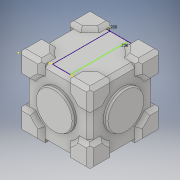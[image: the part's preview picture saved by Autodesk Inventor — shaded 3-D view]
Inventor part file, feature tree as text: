
AUTODESK INVENTOR PART (.ipt)
format: ipt  version: 2018 (Build 220112000, 112)  size: 701,440 bytes
history: native  units: in
note: dims shown in document units (in); Inventor stores cm internally (conversion verified against a paired STEP export)
features: chamfer x100, sketch x16, extrude x15
ambient origin geometry x8: Origin, YZ Plane, XZ Plane, XY Plane, X Axis, Y Axis, Z Axis, Center Point
bodies: Solid1 (feature_tree)
feature tree (131):
  extrude  "Extrusion1"  Depth=4.0in
  extrude  "Extrusion2"  Depth=4.0in
  extrude  "Extrusion3"  Depth=1.3in
  extrude  "Extrusion4"  Depth=1.3in
  extrude  "Extrusion5"  Depth=1.3in
  extrude  "Extrusion6"  Depth=0.2in
  chamfer  "Chamfer42"  Distance=0.2in
  chamfer  "Chamfer43"  Distance=0.2in
  chamfer  "Chamfer44"  Distance=0.2in
  chamfer  "Chamfer45"  Distance=0.2in
  chamfer  "Chamfer46"  Distance=0.2in Angle=45.0deg
  chamfer  "Chamfer47"  Distance=0.2in Angle=45.0deg
  chamfer  "Chamfer48"  Distance=0.2in Angle=45.0deg
  chamfer  "Chamfer49"  Distance=0.2in Angle=45.0deg
  chamfer  "Chamfer50"  Distance=0.2in Angle=45.0deg
  chamfer  "Chamfer51"  Distance=0.2in Angle=45.0deg
  chamfer  "Chamfer52"  Distance=0.2in Angle=45.0deg
  chamfer  "Chamfer53"  Distance=0.2in Angle=45.0deg
  chamfer  "Chamfer54"  Distance=0.2in Angle=45.0deg
  chamfer  "Chamfer55"  Distance=0.2in Angle=45.0deg
  chamfer  "Chamfer56"  Distance=0.2in Angle=45.0deg
  chamfer  "Chamfer57"  Distance=0.2in Angle=45.0deg
  chamfer  "Chamfer58"  Distance=0.2in Angle=45.0deg
  chamfer  "Chamfer59"  Distance=0.2in Angle=45.0deg
  chamfer  "Chamfer60"  Distance=0.2in Angle=45.0deg
  chamfer  "Chamfer61"  Distance=0.2in Angle=45.0deg
  chamfer  "Chamfer62"  Distance=0.2in Angle=45.0deg
  chamfer  "Chamfer63"  Distance=0.2in Angle=45.0deg
  chamfer  "Chamfer64"  Distance=0.2in Angle=45.0deg
  chamfer  "Chamfer65"  Distance=0.2in Angle=45.0deg
  chamfer  "Chamfer66"  Distance=0.2in Angle=45.0deg
  chamfer  "Chamfer67"  Distance=0.2in Angle=45.0deg
  chamfer  "Chamfer68"  Distance=0.2in Angle=45.0deg
  chamfer  "Chamfer69"  Distance=0.2in Angle=45.0deg
  chamfer  "Chamfer70"  Distance=0.2in Angle=45.0deg
  chamfer  "Chamfer71"  Distance=0.2in Angle=45.0deg
  chamfer  "Chamfer72"  Distance=0.2in Angle=45.0deg
  chamfer  "Chamfer73"  Distance=0.2in Angle=45.0deg
  chamfer  "Chamfer74"  Distance=0.2in Angle=45.0deg
  chamfer  "Chamfer75"  Distance=0.2in Angle=45.0deg
  chamfer  "Chamfer76"  Distance=0.2in Angle=45.0deg
  chamfer  "Chamfer77"  Distance=0.2in Angle=45.0deg
  chamfer  "Chamfer78"  Distance=0.2in Angle=45.0deg
  chamfer  "Chamfer79"  Distance=0.2in Angle=45.0deg
  chamfer  "Chamfer80"  Distance=0.2in Angle=45.0deg
  chamfer  "Chamfer81"  Distance=0.2in Angle=45.0deg
  chamfer  "Chamfer82"  Distance=0.2in Angle=45.0deg
  chamfer  "Chamfer83"  Distance=0.2in Angle=45.0deg
  chamfer  "Chamfer84"  Distance=0.2in Angle=45.0deg
  chamfer  "Chamfer85"  Distance=0.2in Angle=45.0deg
  chamfer  "Chamfer86"  Distance=0.2in Angle=45.0deg
  chamfer  "Chamfer87"  Distance=0.2in Angle=45.0deg
  chamfer  "Chamfer88"  Distance=0.2in Angle=45.0deg
  chamfer  "Chamfer89"  Distance=0.2in Angle=45.0deg
  chamfer  "Chamfer90"  Distance=0.2in Angle=45.0deg
  chamfer  "Chamfer91"  Distance=0.2in Angle=45.0deg
  chamfer  "Chamfer92"  Distance=0.2in Angle=45.0deg
  chamfer  "Chamfer93"  Distance=0.2in Angle=45.0deg
  chamfer  "Chamfer94"  Distance=0.2in Angle=45.0deg
  chamfer  "Chamfer95"  Distance=0.2in Angle=45.0deg
  chamfer  "Chamfer96"  Distance=0.2in Angle=45.0deg
  chamfer  "Chamfer97"  Distance=0.2in Angle=45.0deg
  chamfer  "Chamfer98"  Distance=0.2in Angle=45.0deg
  chamfer  "Chamfer99"  Distance=0.2in Angle=45.0deg
  chamfer  "Chamfer100"  Distance=0.2in Angle=45.0deg
  chamfer  "Chamfer101"  Distance=0.2in Angle=45.0deg
  chamfer  "Chamfer102"  Distance=0.2in Angle=45.0deg
  chamfer  "Chamfer103"  Distance=0.2in Angle=45.0deg
  chamfer  "Chamfer104"  Distance=0.2in Angle=45.0deg
  chamfer  "Chamfer105"  Distance=0.2in Angle=45.0deg
  chamfer  "Chamfer106"  Distance=0.2in Angle=45.0deg
  chamfer  "Chamfer107"  Distance=0.2in Angle=45.0deg
  chamfer  "Chamfer108"  Distance=0.2in Angle=45.0deg
  chamfer  "Chamfer109"  Distance=0.2in Angle=45.0deg
  chamfer  "Chamfer110"  Distance=0.2in Angle=45.0deg
  chamfer  "Chamfer111"  Distance=0.2in Angle=45.0deg
  chamfer  "Chamfer112"  Distance=0.2in Angle=45.0deg
  chamfer  "Chamfer113"  Distance=0.2in Angle=45.0deg
  chamfer  "Chamfer114"  Distance=0.2in Angle=45.0deg
  chamfer  "Chamfer115"  Distance=0.2in Angle=45.0deg
  chamfer  "Chamfer116"  Distance=0.2in Angle=45.0deg
  chamfer  "Chamfer117"  Distance=0.2in Angle=45.0deg
  extrude  "Extrusion7"  Depth=0.2in TaperAngle=45.0deg
  extrude  "Extrusion8"  Depth=0.2in TaperAngle=45.0deg
  extrude  "Extrusion9"  Depth=0.2in TaperAngle=0.0deg
  extrude  "Extrusion10"  Depth=0.2in TaperAngle=0.0deg
  chamfer  "Chamfer118"  Distance=0.2in
  chamfer  "Chamfer119"  Distance=0.2in
  chamfer  "Chamfer120"  Distance=0.2in Angle=45.0deg
  chamfer  "Chamfer121"  Distance=0.2in Angle=45.0deg
  chamfer  "Chamfer122"  Distance=0.2in Angle=45.0deg
  chamfer  "Chamfer123"  Distance=0.2in Angle=45.0deg
  chamfer  "Chamfer124"  Distance=0.2in Angle=45.0deg
  chamfer  "Chamfer125"  Distance=0.2in Angle=45.0deg
  chamfer  "Chamfer126"  Distance=0.2in Angle=45.0deg
  chamfer  "Chamfer127"  Distance=0.2in Angle=45.0deg
  chamfer  "Chamfer128"  Distance=0.2in Angle=45.0deg
  chamfer  "Chamfer129"  Distance=0.2in Angle=45.0deg
  chamfer  "Chamfer130"  Distance=0.2in Angle=45.0deg
  chamfer  "Chamfer131"  Distance=0.2in Angle=45.0deg
  chamfer  "Chamfer132"  Distance=0.2in Angle=45.0deg
  chamfer  "Chamfer133"  Distance=0.2in Angle=45.0deg
  extrude  "Extrusion11"  Depth=0.2in TaperAngle=45.0deg
  chamfer  "Chamfer134"  Distance=2.8in
  chamfer  "Chamfer135"  Distance=0.2in
  chamfer  "Chamfer136"  Distance=0.2in Angle=45.0deg
  chamfer  "Chamfer137"  Distance=0.2in Angle=45.0deg
  extrude  "Extrusion12"  Depth=0.2in TaperAngle=45.0deg
  sketch  "Sketch16"  dims[d379=2.8in d380=0.2in d381=0.0in]
  sketch  "Sketch17"  dims[d382=2.8in d383=0.2in d384=0.0in]
  extrude  "Extrusion13"  Depth=0.2in TaperAngle=45.0deg
  extrude  "Extrusion14"  Depth=0.2in
  extrude  "Extrusion15"  Depth=0.2in TaperAngle=0.0deg
  chamfer  "Chamfer138"  Distance=2.1in
  chamfer  "Chamfer139"  Distance=2.1in
  chamfer  "Chamfer140"  Distance=2.1in
  chamfer  "Chamfer141"  Distance=0.2in
  sketch  "Sketch19"  dims[d430=0.2in d431=0.2in d432=45.0deg d433=0.2in d434=0.2in d435=45.0deg d436=2.8in d437=0.2in d438=0.0in d439=0.2in d440=0.2in d441=45.0deg d442=0.2in d443=0.2in d444=45.0deg d445=0.2in d446=0.2in d447=45.0deg d448=0.2in d449=0.2in d450=45.0deg d451=2.1in d452=0.2in d453=0.0in d454=2.1in d455=2.1in d456=2.1in d457=0.2in d458=0.0in d459=0.2in d460=0.0in d461=0.2in d462=0.0in d463=0.05in d464=0.1in d465=45.0deg d466=0.05in d467=0.1in d468=45.0deg d469=0.05in d470=0.1in d471=45.0deg d472=0.05in d473=0.1in d474=45.0deg d475=0.2in d476=0.2in]
  sketch  "Sketch1"  dims[d0=4.0in d1=4.0in]
  sketch  "Sketch2"  dims[d2=4.0in d3=0.0in d4=1.3in]
  sketch  "Sketch3"  dims[d5=1.3in d6=1.3in]
  sketch  "Sketch4"  dims[d7=1.3in d8=1.3in]
  sketch  "Sketch5"  dims[d9=1.3in d10=1.3in]
  sketch  "Sketch6"  dims[d11=0.2in d12=0.0in d13=1.3in]
  sketch  "Sketch9"  dims[d14=1.3in]
  sketch  "Sketch11"  dims[d15=1.3in]
  sketch  "Sketch12"  dims[d16=1.3in d17=0.2in d18=0.0in d19=0.2in d20=0.0in d21=0.2in d22=0.0in d23=0.2in d24=0.0in d148=0.2in d149=0.2in d150=45.0deg d151=0.2in d152=0.2in d153=45.0deg d154=0.2in d155=0.2in d156=45.0deg d157=0.2in d158=0.2in d159=45.0deg d160=0.2in d161=0.2in d162=45.0deg d163=0.2in d164=0.2in d165=45.0deg d166=0.2in d167=0.2in d168=45.0deg d169=0.2in d170=0.2in d171=45.0deg d172=0.2in d173=0.2in d174=45.0deg d175=0.2in d176=0.2in d177=45.0deg d178=0.2in d179=0.2in d180=45.0deg d181=0.2in d182=0.2in d183=45.0deg d184=0.2in d185=0.2in d186=45.0deg d187=0.2in d188=0.2in d189=45.0deg d190=0.2in d191=0.2in d192=45.0deg d193=0.2in d194=0.2in d195=45.0deg d196=0.2in d197=0.2in d198=45.0deg d199=0.2in d200=0.2in d201=45.0deg d202=0.2in d203=0.2in d204=45.0deg d205=0.2in d206=0.2in d207=45.0deg d208=0.2in d209=0.2in d210=45.0deg d211=0.2in d212=0.2in d213=45.0deg d214=0.2in d215=0.2in d216=45.0deg d217=0.2in d218=0.2in d219=45.0deg d220=0.2in d221=0.2in d222=45.0deg d223=0.2in d224=0.2in d225=45.0deg d226=0.2in d227=0.2in d228=45.0deg d229=0.2in d230=0.2in d231=45.0deg d232=0.2in d233=0.2in d234=45.0deg d235=0.2in d236=0.2in d237=45.0deg d238=0.2in d239=0.2in d240=45.0deg d241=0.2in d242=0.2in d243=45.0deg d244=0.2in d245=0.2in d246=45.0deg d247=0.2in d248=0.2in d249=45.0deg d250=0.2in d251=0.2in d252=45.0deg d253=0.2in d254=0.2in d255=45.0deg d256=0.2in d257=0.2in d258=45.0deg d259=0.2in d260=0.2in d261=45.0deg d262=0.2in d263=0.2in d264=45.0deg d265=0.2in d266=0.2in d267=45.0deg d268=0.2in d269=0.2in d270=45.0deg d271=0.2in d272=0.2in d273=45.0deg d274=0.2in d275=0.2in d276=45.0deg d277=0.2in d278=0.2in d279=45.0deg d280=0.2in d281=0.2in d282=45.0deg d283=0.2in d284=0.2in d285=45.0deg d286=0.2in d287=0.2in d288=45.0deg d289=0.2in d290=0.2in d291=45.0deg d292=0.2in d293=0.2in d294=45.0deg d295=0.2in d296=0.2in d297=45.0deg d298=0.2in d299=0.2in d300=45.0deg d301=0.2in d302=0.2in d303=45.0deg d304=0.2in d305=0.2in d306=45.0deg d307=0.2in d308=0.2in d309=45.0deg d310=0.2in d311=0.2in d312=45.0deg d313=0.2in d314=0.2in d315=45.0deg d316=0.2in d317=0.2in d318=45.0deg d319=0.2in d320=0.2in d321=45.0deg d322=0.2in d323=0.2in d324=45.0deg d325=0.2in d326=0.2in d327=45.0deg d328=0.2in d329=0.2in d330=45.0deg d331=0.2in d332=0.2in d333=45.0deg d334=0.2in d335=0.2in d336=45.0deg d337=0.2in d338=0.2in d339=45.0deg d340=0.2in d341=0.2in d342=45.0deg d343=0.2in d344=0.2in d345=45.0deg d346=0.2in d347=0.2in d348=45.0deg d349=0.2in d350=0.2in d351=45.0deg d352=0.2in d353=0.2in d354=45.0deg d355=0.2in d356=0.2in d357=45.0deg d358=0.2in d359=0.2in d360=45.0deg d361=0.2in d362=0.2in d363=45.0deg]
  sketch  "Sketch13"  dims[d364=0.2in d365=0.2in d366=45.0deg d367=0.2in d368=0.2in d369=45.0deg]
  sketch  "Sketch14"  dims[d370=0.2in d371=0.2in d372=45.0deg d373=0.2in d374=0.2in d375=45.0deg]
  sketch  "Sketch15"  dims[d376=2.8in d377=0.2in d378=0.0in]
  sketch  "Sketch18"  dims[d385=2.8in d386=0.2in d387=0.0in d388=0.2in d389=0.2in d390=45.0deg d391=0.2in d392=0.2in d393=45.0deg d394=0.2in d395=0.2in d396=45.0deg d397=0.2in d398=0.2in d399=45.0deg d400=0.2in d401=0.2in d402=45.0deg d403=0.2in d404=0.2in d405=45.0deg d406=0.2in d407=0.2in d408=45.0deg d409=0.2in d410=0.2in d411=45.0deg d412=0.2in d413=0.2in d414=45.0deg d415=0.2in d416=0.2in d417=45.0deg d418=0.2in d419=0.2in d420=45.0deg d421=0.2in d422=0.2in d423=45.0deg d424=0.2in d425=0.2in d426=45.0deg d427=0.2in d428=0.2in d429=45.0deg]
